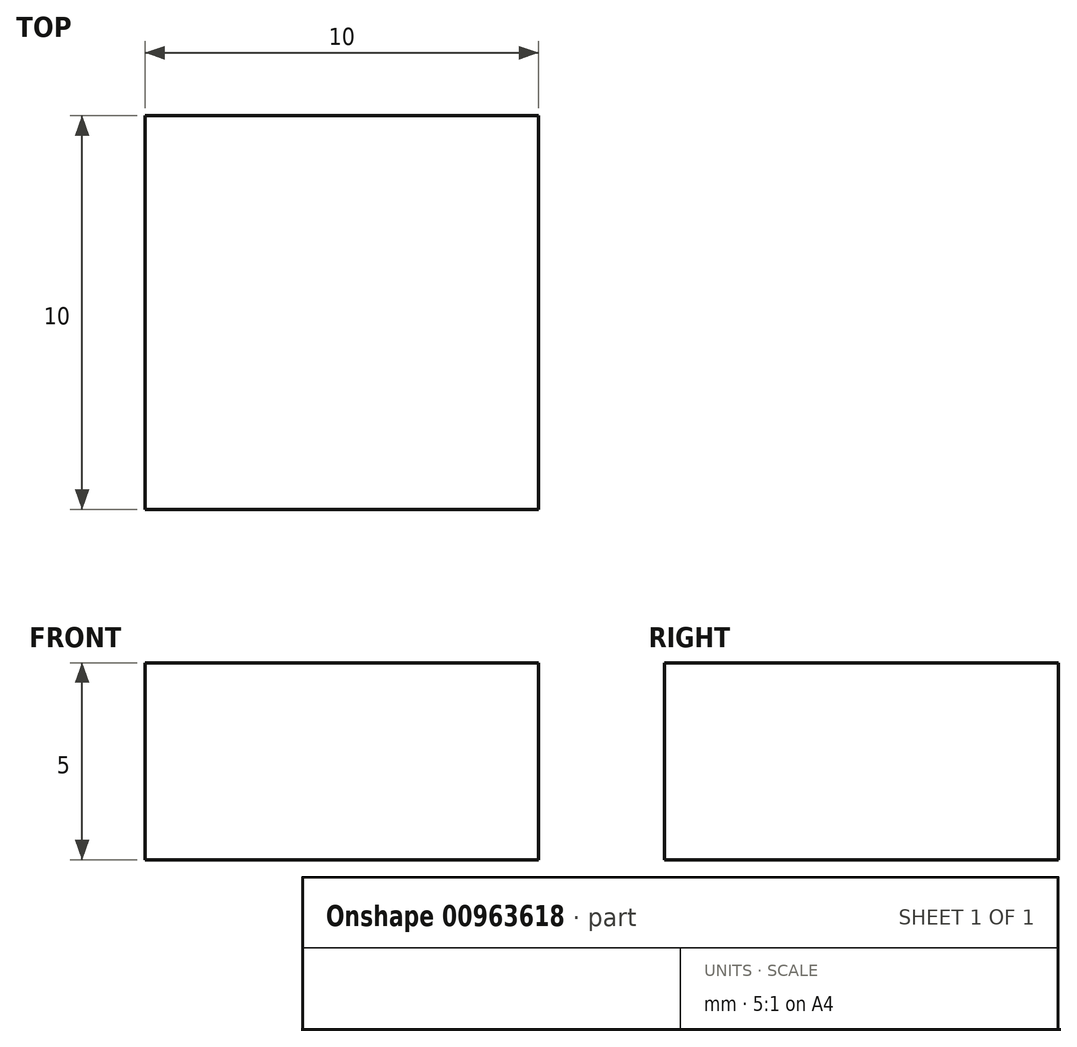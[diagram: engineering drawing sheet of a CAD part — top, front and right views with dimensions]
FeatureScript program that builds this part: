
annotation { "Feature Type Name" : "Feature", "Feature Type Description" : "" }
export const myFeature = defineFeature(function(context is Context, id is Id, definition is map)
    precondition{}
    {
        {
            var Q0;
            Q0=qCreatedBy(makeId("Top.planeOp"),FACE);
            var sketch = newSketch(context, id + "F0", { "sketchPlane" : qUnion([Q0])});
            skLineSegment(sketch, "E0.bottom", {"start": v(0, 0) * mm, "end": v(-10, 0) * mm});
            skLineSegment(sketch, "E0.top", {"start": v(0, -10) * mm, "end": v(-10, -10) * mm});
            skLineSegment(sketch, "E0.left", {"start": v(0, 0) * mm, "end": v(0, -10) * mm});
            skLineSegment(sketch, "E0.right", {"start": v(-10, 0) * mm, "end": v(-10, -10) * mm});
            skSolve(sketch);
        }
        {
            var Q0;
            Q0=makeQuery(id+"F0.imprint","IMPRINT",FACE,{"disambiguationData":[TD([[makeQuery(id+"F0.imprint","IMPRINT",EDGE,{"derivedFrom":sQuery(id+"F0.wireOp",EDGE,"E0.bottom")}),1.0]])]});
            extrude(context, id + "F1", {"entities" : qUnion([Q0]), "depth" : 5 * mm, "offsetDistance" : 25 * mm});
        }
    });
